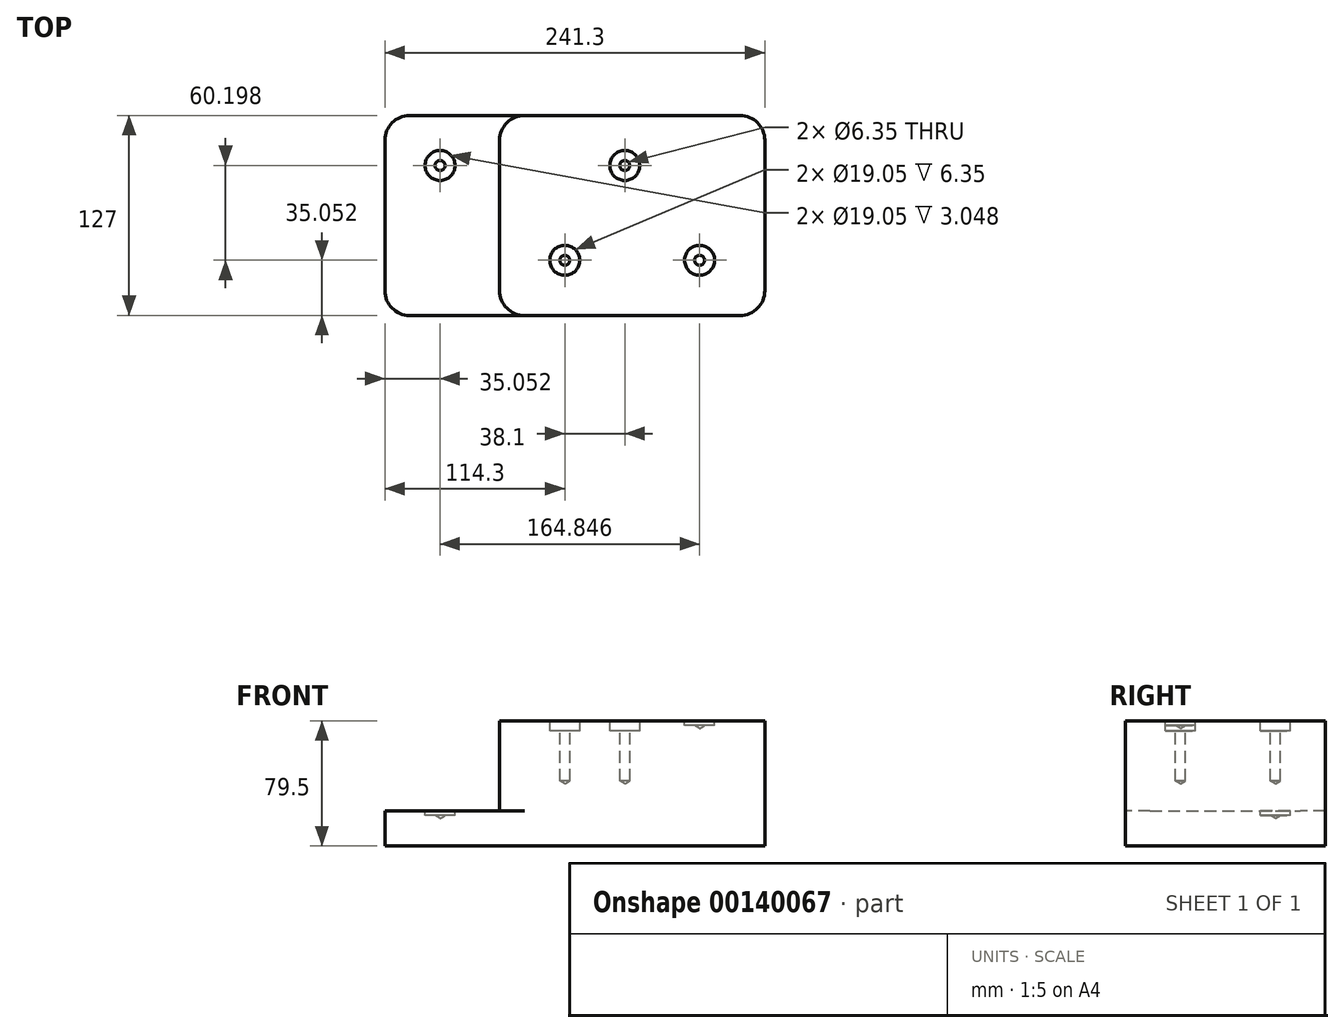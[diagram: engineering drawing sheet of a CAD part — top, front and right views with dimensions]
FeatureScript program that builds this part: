
annotation { "Feature Type Name" : "Feature", "Feature Type Description" : "" }
export const myFeature = defineFeature(function(context is Context, id is Id, definition is map)
    precondition{}
    {
        {
            var Q0;
            Q0=qCreatedBy(makeId("Front.planeOp"),FACE);
            var sketch = newSketch(context, id + "F0", { "sketchPlane" : qUnion([Q0])});
            skLineSegment(sketch, "E0", {"start": v(0, 0) * mm, "end": v(0, 22.35) * mm});
            skLineSegment(sketch, "E1", {"start": v(0, 22.35) * mm, "end": v(72.9, 22.35) * mm});
            skLineSegment(sketch, "E2", {"start": v(72.9, 22.35) * mm, "end": v(72.9, 79.5) * mm});
            skLineSegment(sketch, "E3", {"start": v(72.9, 79.5) * mm, "end": v(241.3, 79.5) * mm});
            skLineSegment(sketch, "E4", {"start": v(241.3, 79.5) * mm, "end": v(241.3, 0) * mm});
            skLineSegment(sketch, "E5", {"start": v(241.3, 0) * mm, "end": v(0, 0) * mm});
            skSolve(sketch);
        }
        {
            var Q0;
            Q0 = qSketchRegion(id + "F0", true);
            extrude(context, id + "F1", {"entities" : qUnion([Q0]), "depth" : 127 * mm});
        }
        {
            var Q0;
            Q0=makeQuery(id+"F1.opExtrude","CAP_EDGE",EDGE,{"disambiguationData":[OSD([sQuery(id+"F0.wireOp",EDGE,"E0")])],"isStart":false});
            var Q1;
            Q1=makeQuery(id+"F1.opExtrude","CAP_EDGE",EDGE,{"disambiguationData":[OSD([sQuery(id+"F0.wireOp",EDGE,"E0")])],"isStart":true});
            var Q2;
            Q2=makeQuery(id+"F1.opExtrude","CAP_EDGE",EDGE,{"disambiguationData":[OSD([sQuery(id+"F0.wireOp",EDGE,"E2")])],"isStart":false});
            var Q3;
            Q3=makeQuery(id+"F1.opExtrude","CAP_EDGE",EDGE,{"disambiguationData":[OSD([sQuery(id+"F0.wireOp",EDGE,"E2")])],"isStart":true});
            var Q4;
            Q4=makeQuery(id+"F1.opExtrude","CAP_EDGE",EDGE,{"disambiguationData":[OSD([sQuery(id+"F0.wireOp",EDGE,"E4")])],"isStart":false});
            var Q5;
            Q5=makeQuery(id+"F1.opExtrude","CAP_EDGE",EDGE,{"disambiguationData":[OSD([sQuery(id+"F0.wireOp",EDGE,"E4")])],"isStart":true});
            fillet(context, id + "F2", {"entities" : qUnion([Q0, Q1, Q2, Q3, Q4, Q5]), "radius" : 15.75 * mm, "tangentPropagation" : true, "allowEdgeOverflow" : false});
        }
        {
            var Q0;
            Q0=makeQuery(id+"F1.opExtrude","SWEPT_FACE",FACE,{"disambiguationData":[OSD([sQuery(id+"F0.wireOp",EDGE,"E3")])]});
            var sketch = newSketch(context, id + "F3", { "sketchPlane" : qUnion([Q0])});
            skPoint(sketch, "E6", {"position": v(114.3, -91.95) * mm});
            skPoint(sketch, "E7", {"position": v(152.4, -31.75) * mm});
            skPoint(sketch, "E8", {"position": v(199.9, -91.95) * mm});
            skPoint(sketch, "E9", {"position": v(35.05, -31.75) * mm});
            skCircle(sketch, "E10", {"center": v(35.05, -31.75) * mm, "radius": 9.53 * mm});
            skCircle(sketch, "E11", {"center": v(152.4, -31.75) * mm, "radius": 9.53 * mm});
            skCircle(sketch, "E12", {"center": v(114.3, -91.95) * mm, "radius": 9.53 * mm});
            skCircle(sketch, "E13", {"center": v(199.9, -91.95) * mm, "radius": 9.53 * mm});
            skSolve(sketch);
        }
        {
            var Q0;
            Q0=sQuery(id+"F3.wireOp",VERTEX,"E7");
            var Q1;
            Q1=sQuery(id+"F3.wireOp",VERTEX,"E6");
            var Q2;
            Q2=makeQuery(id+"F1.opExtrude","SWEPT_BODY",BODY,{"disambiguationData":[OSD([sQuery(id+"F0.wireOp",EDGE,"E0"),sQuery(id+"F0.wireOp",EDGE,"E1"),sQuery(id+"F0.wireOp",EDGE,"E2"),sQuery(id+"F0.wireOp",EDGE,"E3"),sQuery(id+"F0.wireOp",EDGE,"E4"),sQuery(id+"F0.wireOp",EDGE,"E5")])]});
            hole(context, id + "F4", {"style" : HoleStyle.C_BORE, "endStyle" : HoleEndStyle.BLIND, "holeDiameter" : 6.35 * mm, "cBoreDiameter" : 19.05 * mm, "cBoreDepth" : 6.35 * mm, "holeDepth" : 38.1 * mm, "locations" : qUnion([Q0, Q1]), "scope" : qUnion([Q2])});
        }
        {
            var Q0;
            Q0=sQuery(id+"F3.wireOp",VERTEX,"E8");
            var Q1;
            Q1=sQuery(id+"F3.wireOp",VERTEX,"E9");
            var Q2;
            Q2=makeQuery(id+"F1.opExtrude","SWEPT_BODY",BODY,{"disambiguationData":[OSD([sQuery(id+"F0.wireOp",EDGE,"E0"),sQuery(id+"F0.wireOp",EDGE,"E1"),sQuery(id+"F0.wireOp",EDGE,"E2"),sQuery(id+"F0.wireOp",EDGE,"E3"),sQuery(id+"F0.wireOp",EDGE,"E4"),sQuery(id+"F0.wireOp",EDGE,"E5")])]});
            hole(context, id + "F5", {"style" : HoleStyle.C_BORE, "endStyle" : HoleEndStyle.BLIND, "holeDiameter" : 6.35 * mm, "cBoreDiameter" : 19.05 * mm, "cBoreDepth" : 3.05 * mm, "holeDepth" : 3.05 * mm, "locations" : qUnion([Q0, Q1]), "scope" : qUnion([Q2])});
        }
    });
